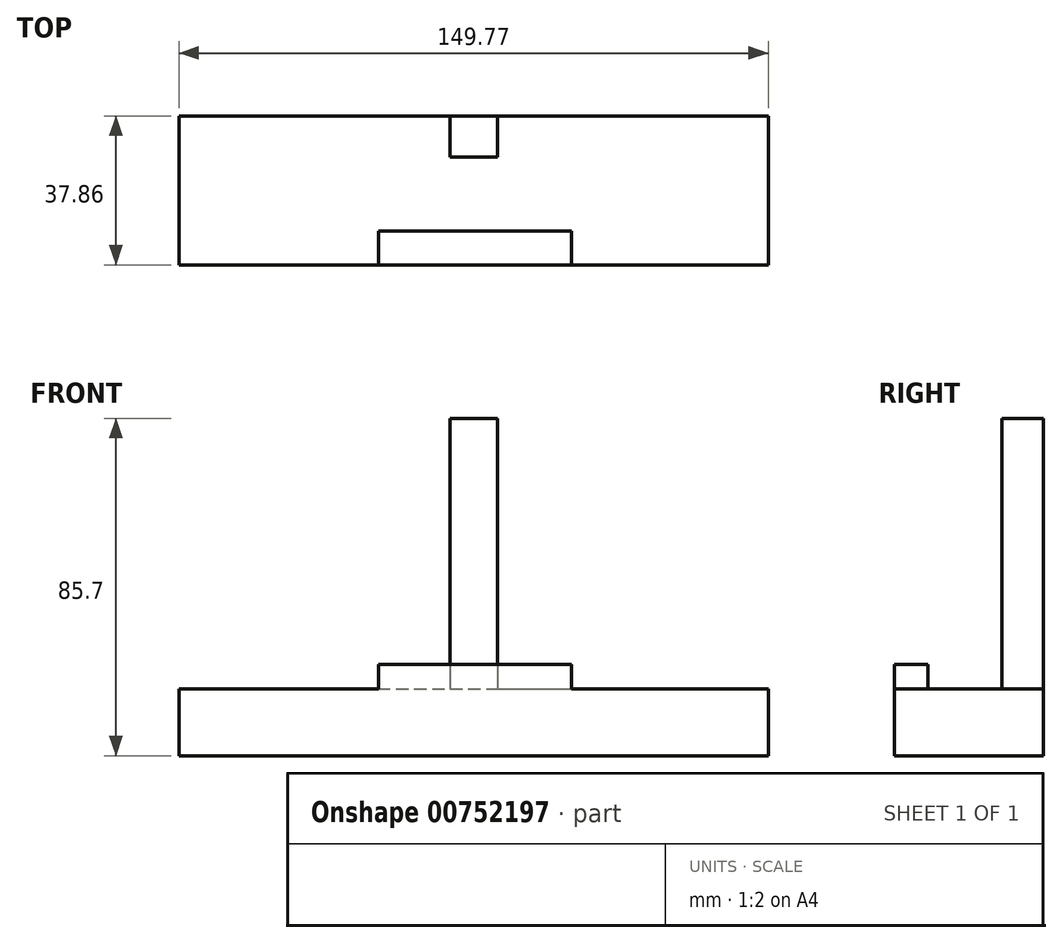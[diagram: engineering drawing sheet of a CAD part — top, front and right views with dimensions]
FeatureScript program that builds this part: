
annotation { "Feature Type Name" : "Feature", "Feature Type Description" : "" }
export const myFeature = defineFeature(function(context is Context, id is Id, definition is map)
    precondition{}
    {
        {
            var Q0;
            Q0=qCreatedBy(makeId("Top.planeOp"),FACE);
            var sketch = newSketch(context, id + "F0", { "sketchPlane" : qUnion([Q0])});
            skLineSegment(sketch, "E0.bottom", {"start": v(-75.02, 19.24) * mm, "end": v(74.75, 19.24) * mm});
            skLineSegment(sketch, "E0.top", {"start": v(-75.02, -18.62) * mm, "end": v(74.75, -18.62) * mm});
            skLineSegment(sketch, "E0.left", {"start": v(-75.02, 19.24) * mm, "end": v(-75.02, -18.62) * mm});
            skLineSegment(sketch, "E0.right", {"start": v(74.75, 19.24) * mm, "end": v(74.75, -18.62) * mm});
            skSolve(sketch);
        }
        {
            var Q0;
            Q0 = qSketchRegion(id + "F0", true);
            extrude(context, id + "F1", {"entities" : qUnion([Q0]), "depth" : 17 * mm, "offsetDistance" : 25 * mm});
        }
        {
            var Q0;
            Q0=makeQuery(id+"F1.opExtrude","CAP_FACE",FACE,{"disambiguationData":[OSD([sQuery(id+"F0.wireOp",EDGE,"E0.bottom"),sQuery(id+"F0.wireOp",EDGE,"E0.top"),sQuery(id+"F0.wireOp",EDGE,"E0.left"),sQuery(id+"F0.wireOp",EDGE,"E0.right")])],"isStart":false});
            var sketch = newSketch(context, id + "F2", { "sketchPlane" : qUnion([Q0])});
            skLineSegment(sketch, "E1.bottom", {"start": v(-6.1, 19.24) * mm, "end": v(5.94, 19.24) * mm});
            skLineSegment(sketch, "E1.top", {"start": v(-6.1, 8.72) * mm, "end": v(5.94, 8.72) * mm});
            skLineSegment(sketch, "E1.left", {"start": v(-6.1, 19.24) * mm, "end": v(-6.1, 8.72) * mm});
            skLineSegment(sketch, "E1.right", {"start": v(5.94, 19.24) * mm, "end": v(5.94, 8.72) * mm});
            skLineSegment(sketch, "E2.bottom", {"start": v(-24.33, -18.62) * mm, "end": v(24.77, -18.62) * mm});
            skLineSegment(sketch, "E2.top", {"start": v(-24.33, -10.04) * mm, "end": v(24.77, -10.04) * mm});
            skLineSegment(sketch, "E2.left", {"start": v(-24.33, -18.62) * mm, "end": v(-24.33, -10.04) * mm});
            skLineSegment(sketch, "E2.right", {"start": v(24.77, -18.62) * mm, "end": v(24.77, -10.04) * mm});
            skSolve(sketch);
        }
        {
            var Q0;
            Q0=makeQuery(id+"F2.imprint","IMPRINT",FACE,{"disambiguationData":[TD([[makeQuery(id+"F2.imprint","IMPRINT",EDGE,{"derivedFrom":sQuery(id+"F2.wireOp",EDGE,"E1.bottom")}),-1.0]])]});
            extrude(context, id + "F3", {"entities" : qUnion([Q0]), "operationType" : NewBodyOperationType.ADD, "depth" : 68.7 * mm, "offsetDistance" : 25 * mm});
        }
        {
            var Q0;
            Q0=makeQuery(id+"F2.imprint","IMPRINT",FACE,{"disambiguationData":[TD([[makeQuery(id+"F2.imprint","IMPRINT",EDGE,{"derivedFrom":sQuery(id+"F2.wireOp",EDGE,"E2.bottom")}),1.0]])]});
            extrude(context, id + "F4", {"entities" : qUnion([Q0]), "operationType" : NewBodyOperationType.ADD, "depth" : 6.2 * mm, "offsetDistance" : 25 * mm});
        }
    });
